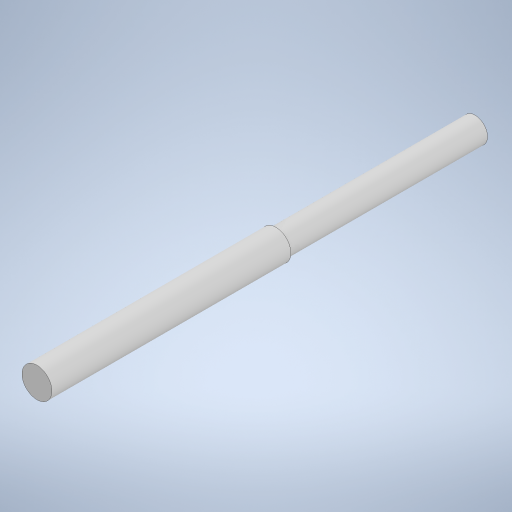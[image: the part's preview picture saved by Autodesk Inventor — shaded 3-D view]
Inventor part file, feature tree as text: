
AUTODESK INVENTOR PART (.ipt)
format: ipt  version: 2023 (Build 270158000, 158)  size: 241,152 bytes
history: native  units: mm
features: extrude x3, sketch x3
ambient origin geometry x8: Origin, YZ Plane, XZ Plane, XY Plane, X Axis, Y Axis, Z Axis, Center Point
bodies: Solid1 (feature_tree)
feature tree (6):
  extrude  "Extrusion1"  Depth=4.0mm TaperAngle=0.0deg
  extrude  "Extrusion2"  Depth=20.0mm TaperAngle=0.0deg
  extrude  "Extrusion3"  Depth=20.0mm TaperAngle=0.0deg
  sketch  "Sketch1"  dims[d0=3.0mm d1=4.0mm d2=0.0mm]
  sketch  "Sketch2"  dims[d3=3.0mm d4=20.0mm d5=0.0mm]
  sketch  "Sketch3"  dims[d8=2.5mm d9=20.0mm d10=0.0mm]
